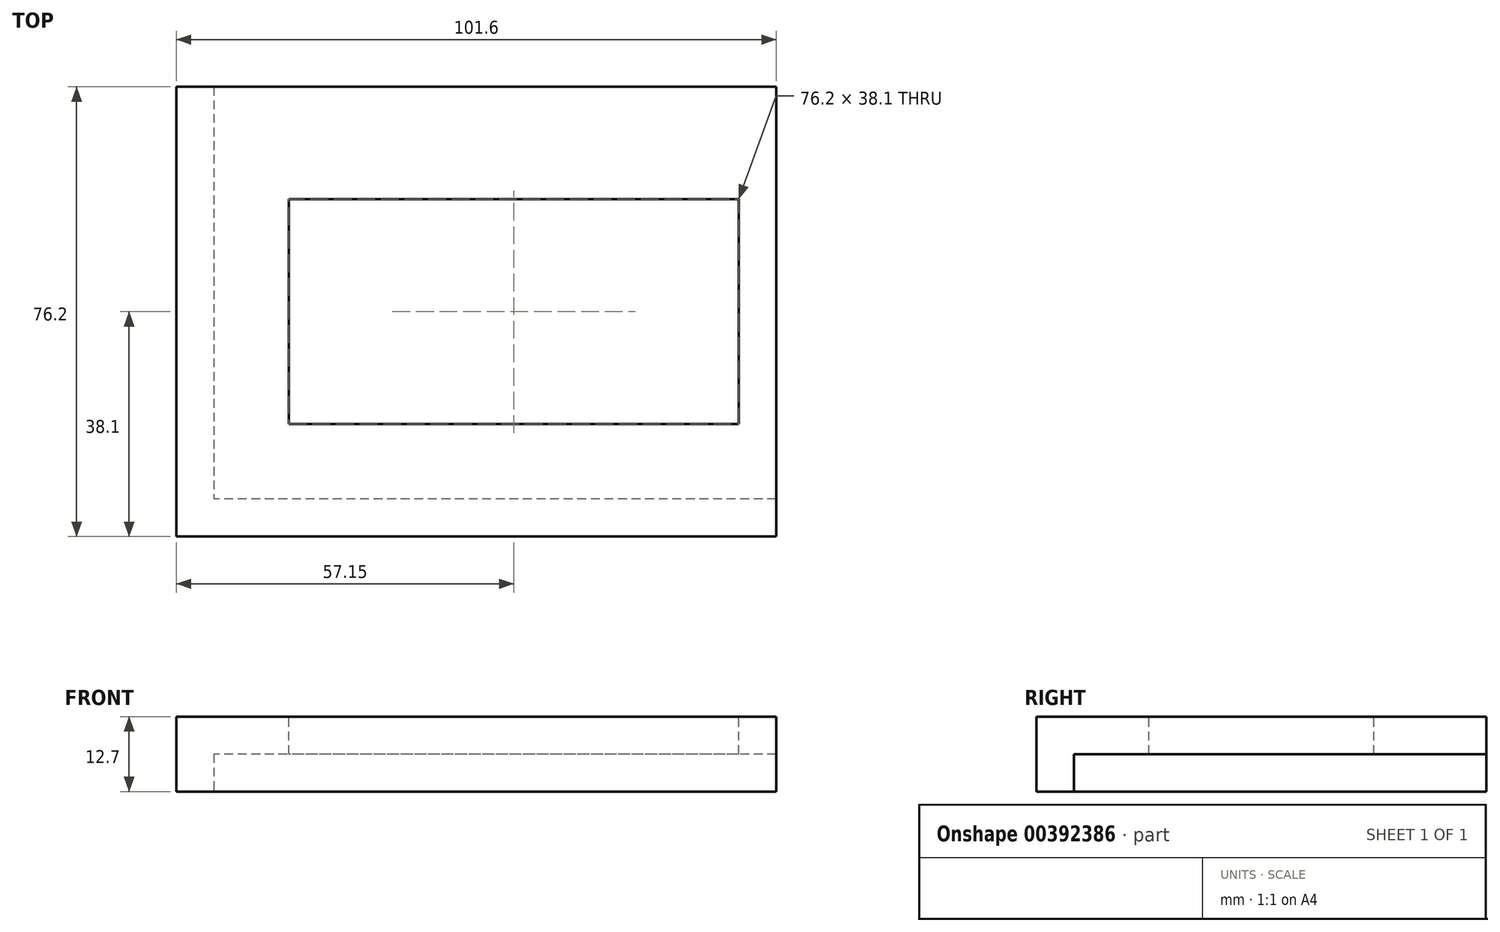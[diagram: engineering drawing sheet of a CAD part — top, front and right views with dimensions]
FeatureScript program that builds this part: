
annotation { "Feature Type Name" : "Feature", "Feature Type Description" : "" }
export const myFeature = defineFeature(function(context is Context, id is Id, definition is map)
    precondition{}
    {
        {
            var Q0;
            Q0=qCreatedBy(makeId("Top.planeOp"),FACE);
            var sketch = newSketch(context, id + "F0", { "sketchPlane" : qUnion([Q0])});
            skLineSegment(sketch, "E0.bottom", {"start": v(50.8, -38.1) * mm, "end": v(-50.8, -38.1) * mm});
            skLineSegment(sketch, "E0.top", {"start": v(50.8, 38.1) * mm, "end": v(-50.8, 38.1) * mm});
            skLineSegment(sketch, "E0.left", {"start": v(50.8, -38.1) * mm, "end": v(50.8, 38.1) * mm});
            skLineSegment(sketch, "E0.right", {"start": v(-50.8, -38.1) * mm, "end": v(-50.8, 38.1) * mm});
            skPoint(sketch, "E0.middle", {"position": v(0, 0) * mm});
            skSolve(sketch);
        }
        {
            var Q0;
            Q0=makeQuery(id+"F0.imprint","IMPRINT",FACE,{"disambiguationData":[TD([[makeQuery(id+"F0.imprint","IMPRINT",EDGE,{"derivedFrom":sQuery(id+"F0.wireOp",EDGE,"E0.bottom")}),-1.0]])]});
            extrude(context, id + "F1", {"entities" : qUnion([Q0]), "depth" : 12.7 * mm});
        }
        {
            var Q0;
            Q0=makeQuery(id+"F1.opExtrude","CAP_FACE",FACE,{"disambiguationData":[OSD([sQuery(id+"F0.wireOp",EDGE,"E0.bottom"),sQuery(id+"F0.wireOp",EDGE,"E0.top"),sQuery(id+"F0.wireOp",EDGE,"E0.left"),sQuery(id+"F0.wireOp",EDGE,"E0.right")])],"isStart":true});
            var sketch = newSketch(context, id + "F2", { "sketchPlane" : qUnion([Q0])});
            skLineSegment(sketch, "E1.bottom", {"start": v(50.8, -38.1) * mm, "end": v(-44.45, -38.1) * mm});
            skLineSegment(sketch, "E1.top", {"start": v(50.8, 31.75) * mm, "end": v(-44.45, 31.75) * mm});
            skLineSegment(sketch, "E1.left", {"start": v(50.8, -38.1) * mm, "end": v(50.8, 31.75) * mm});
            skLineSegment(sketch, "E1.right", {"start": v(-44.45, -38.1) * mm, "end": v(-44.45, 31.75) * mm});
            skSolve(sketch);
        }
        {
            var Q0;
            Q0=makeQuery(id+"F2.imprint","IMPRINT",FACE,{"disambiguationData":[TD([[makeQuery(id+"F2.imprint","IMPRINT",EDGE,{"derivedFrom":sQuery(id+"F2.wireOp",EDGE,"E1.bottom")}),-1.0]])]});
            extrude(context, id + "F3", {"entities" : qUnion([Q0]), "operationType" : NewBodyOperationType.REMOVE, "oppositeDirection" : true, "depth" : 6.35 * mm});
        }
        {
            var Q0;
            Q0=makeQuery(id+"F1.opExtrude","CAP_FACE",FACE,{"disambiguationData":[OSD([sQuery(id+"F0.wireOp",EDGE,"E0.bottom"),sQuery(id+"F0.wireOp",EDGE,"E0.top"),sQuery(id+"F0.wireOp",EDGE,"E0.left"),sQuery(id+"F0.wireOp",EDGE,"E0.right")])],"isStart":false});
            var sketch = newSketch(context, id + "F4", { "sketchPlane" : qUnion([Q0])});
            skLineSegment(sketch, "E2.bottom", {"start": v(-31.75, -19.05) * mm, "end": v(44.45, -19.05) * mm});
            skLineSegment(sketch, "E2.top", {"start": v(-31.75, 19.05) * mm, "end": v(44.45, 19.05) * mm});
            skLineSegment(sketch, "E2.left", {"start": v(-31.75, -19.05) * mm, "end": v(-31.75, 19.05) * mm});
            skLineSegment(sketch, "E2.right", {"start": v(44.45, -19.05) * mm, "end": v(44.45, 19.05) * mm});
            skSolve(sketch);
        }
        {
            var Q0;
            Q0=makeQuery(id+"F4.imprint","IMPRINT",FACE,{"disambiguationData":[TD([[makeQuery(id+"F4.imprint","IMPRINT",EDGE,{"derivedFrom":sQuery(id+"F4.wireOp",EDGE,"E2.bottom")}),1.0]])]});
            extrude(context, id + "F5", {"entities" : qUnion([Q0]), "operationType" : NewBodyOperationType.REMOVE, "oppositeDirection" : true, "depth" : 25.4 * mm});
        }
    });
